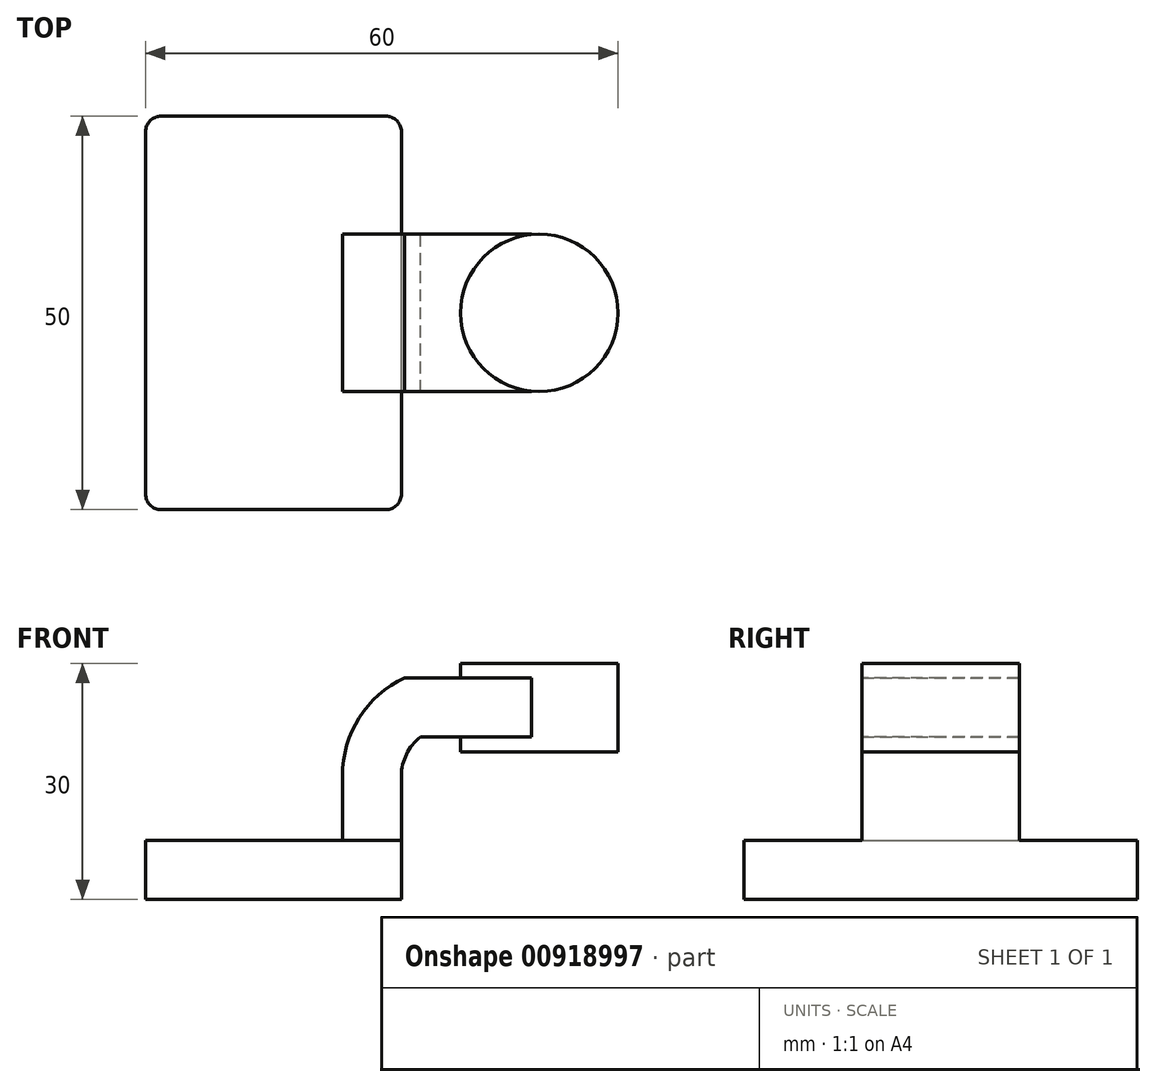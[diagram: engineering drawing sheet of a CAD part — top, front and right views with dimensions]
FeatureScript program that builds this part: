
annotation { "Feature Type Name" : "Feature", "Feature Type Description" : "" }
export const myFeature = defineFeature(function(context is Context, id is Id, definition is map)
    precondition{}
    {
        {
            var Q0;
            Q0=qCreatedBy(makeId("Front.planeOp"),FACE);
            var sketch = newSketch(context, id + "F0", { "sketchPlane" : qUnion([Q0])});
            skLineSegment(sketch, "E0.bottom", {"start": v(-16.25, 3.75) * mm, "end": v(16.25, 3.75) * mm});
            skLineSegment(sketch, "E0.top", {"start": v(-16.25, -3.75) * mm, "end": v(16.25, -3.75) * mm});
            skLineSegment(sketch, "E0.left", {"start": v(-16.25, 3.75) * mm, "end": v(-16.25, -3.75) * mm});
            skLineSegment(sketch, "E0.right", {"start": v(16.25, 3.75) * mm, "end": v(16.25, -3.75) * mm});
            skPoint(sketch, "E0.middle", {"position": v(0, 0) * mm});
            skLineSegment(sketch, "E1.bottom", {"start": v(43.75, 15) * mm, "end": v(23.75, 15) * mm});
            skLineSegment(sketch, "E1.top", {"start": v(43.75, 26.25) * mm, "end": v(23.75, 26.25) * mm});
            skLineSegment(sketch, "E1.left", {"start": v(43.75, 15) * mm, "end": v(43.75, 26.25) * mm});
            skLineSegment(sketch, "E1.right", {"start": v(23.75, 15) * mm, "end": v(23.75, 26.25) * mm});
            skPoint(sketch, "E1.middle", {"position": v(33.75, 20.62) * mm});
            skLineSegment(sketch, "E2", {"start": v(16.25, 3.75) * mm, "end": v(16.25, 11.95) * mm});
            skLineSegment(sketch, "E3", {"start": v(18.66, 16.88) * mm, "end": v(32.77, 16.88) * mm});
            skArc(sketch, "E4", {"start": v(16.25, 11.95) * mm, "mid": v(16.88, 14.7) * mm, "end": v(18.66, 16.88) * mm});
            skLineSegment(sketch, "E5.0", {"start": v(16.62, 24.38) * mm, "end": v(32.77, 24.38) * mm});
            skArc(sketch, "E5.1", {"start": v(8.75, 11.95) * mm, "mid": v(10.88, 19.3) * mm, "end": v(16.62, 24.38) * mm});
            skLineSegment(sketch, "E5.2", {"start": v(8.75, 3.75) * mm, "end": v(8.75, 11.95) * mm});
            skLineSegment(sketch, "E6", {"start": v(32.77, 16.88) * mm, "end": v(32.77, 24.38) * mm});
            skFitSpline(sketch, "E7", {"points": [v(-16.25, 3.75) * mm, v(16.62, 24.38) * mm], "startDerivative": vector(23.22, 45.7) * mm, "endDerivative": vector(38.43, 1.92) * mm});
            skLineSegment(sketch, "E8", {"start": v(33.75, 20.62) * mm, "end": v(33.75, 26.25) * mm});
            skLineSegment(sketch, "E9", {"start": v(33.75, 20.62) * mm, "end": v(33.75, 15) * mm});
            skLineSegment(sketch, "E10", {"start": v(32.77, 24.38) * mm, "end": v(33.75, 24.38) * mm});
            skLineSegment(sketch, "E11", {"start": v(32.77, 16.88) * mm, "end": v(33.75, 16.88) * mm});
            skSolve(sketch);
        }
        {
            var Q0;
            Q0=makeQuery(id+"F0.imprint","IMPRINT",FACE,{"disambiguationData":[TD([[makeQuery(id+"F0.imprint","IMPRINT",EDGE,{"derivedFrom":sQuery(id+"F0.wireOp",EDGE,"E0.top")}),1.0]])]});
            extrude(context, id + "F1", {"entities" : qUnion([Q0]), "endBound" : BoundingType.SYMMETRIC, "depth" : 50 * mm, "offsetDistance" : 25 * mm});
        }
        {
            var Q0;
            {var subQ4=sQuery(id+"F0.wireOp",EDGE,"E2");Q0=makeQuery(id+"F0.imprint","IMPRINT",FACE,{"disambiguationData":[TD([[makeQuery(id+"F0.imprint","IMPRINT",EDGE,{"derivedFrom":subQ4}),1.0]])]});}
            var Q1;
            {var subQ5=sQuery(id+"F0.wireOp",EDGE,"E6");Q1=makeQuery(id+"F0.imprint","IMPRINT",FACE,{"disambiguationData":[TD([[makeQuery(id+"F0.imprint","IMPRINT",EDGE,{"derivedFrom":subQ5}),1.0]])]});}
            extrude(context, id + "F2", {"entities" : qUnion([Q0, Q1]), "operationType" : NewBodyOperationType.ADD, "endBound" : BoundingType.SYMMETRIC, "depth" : 20 * mm, "offsetDistance" : 25 * mm});
        }
        {
            var Q0;
            Q0=makeQuery(id+"F0.imprint","IMPRINT",FACE,{"disambiguationData":[TD([[makeQuery(id+"F0.imprint","IMPRINT",EDGE,{"derivedFrom":sQuery(id+"F0.wireOp",EDGE,"E5.1")}),1.0]])]});
            extrude(context, id + "F3", {"entities" : qUnion([Q0]), "operationType" : NewBodyOperationType.ADD, "endBound" : BoundingType.SYMMETRIC, "depth" : 6.25 * mm, "offsetDistance" : 25 * mm});
        }
        {
            var Q0;
            {var subQ4=sQuery(id+"F0.wireOp",EDGE,"E1.left");Q0=makeQuery(id+"F0.imprint","IMPRINT",FACE,{"disambiguationData":[TD([[makeQuery(id+"F0.imprint","IMPRINT",EDGE,{"derivedFrom":subQ4}),1.0]])]});}
            var Q1;
            Q1=sQuery(id+"F0.wireOp",EDGE,"E8");
            revolve(context, id + "F4", {"operationType" : NewBodyOperationType.ADD, "surfaceOperationType" : NewSurfaceOperationType.NEW, "entities" : qUnion([Q0]), "axis" : qUnion([Q1]), "revolveType" : RevolveType.FULL});
        }
        {
            var Q0;
            Q0=makeQuery(id+"F1.opExtrude","CAP_EDGE",EDGE,{"disambiguationData":[OSD([sQuery(id+"F0.wireOp",EDGE,"E0.left")])],"isStart":true});
            var Q1;
            Q1=makeQuery(id+"F1.opExtrude","CAP_EDGE",EDGE,{"disambiguationData":[OSD([sQuery(id+"F0.wireOp",EDGE,"E0.left")])],"isStart":false});
            var Q2;
            Q2=makeQuery(id+"F1.opExtrude","CAP_EDGE",EDGE,{"disambiguationData":[OSD([sQuery(id+"F0.wireOp",EDGE,"E0.right")])],"isStart":false});
            var Q3;
            Q3=makeQuery(id+"F1.opExtrude","CAP_EDGE",EDGE,{"disambiguationData":[OSD([sQuery(id+"F0.wireOp",EDGE,"E0.right")])],"isStart":true});
            fillet(context, id + "F5", {"entities" : qUnion([Q0, Q1, Q2, Q3]), "radius" : 2 * mm, "tangentPropagation" : true, "allowEdgeOverflow" : false});
        }
    });
